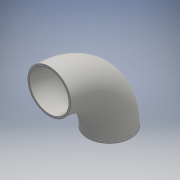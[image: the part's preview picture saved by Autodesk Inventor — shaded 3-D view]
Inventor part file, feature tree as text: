
AUTODESK INVENTOR PART (.ipt)
format: ipt  version: 2016 (Build 200138000, 138)  size: 149,504 bytes
history: native  units: mm
features: sweep x1, sketch x1
ambient origin geometry x8: Origin, YZ Plane, XZ Plane, XY Plane, X Axis, Y Axis, Z Axis, Center Point
bodies: Body1 (feature_tree)
feature tree (2):
  sweep  "Sweep6"
  sketch  "Sketch4"  dims[d23=305.0mm d27=219.0mm d28=9.57mm d29=0.0mm d30=0.0mm]
